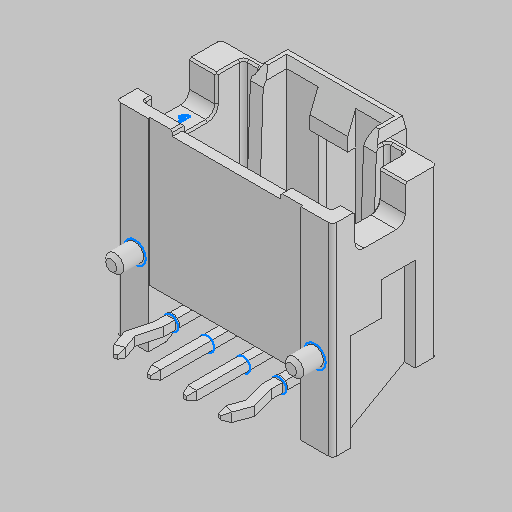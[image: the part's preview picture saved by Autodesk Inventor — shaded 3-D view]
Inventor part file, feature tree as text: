
AUTODESK INVENTOR PART (.ipt)
format: ipt  version: 2023.5 (Build 275446000, 446)  size: 349,696 bytes
history: native  units: in
note: dims shown in document units (in); Inventor stores cm internally (conversion verified against a paired STEP export)
features: other x1, extrude x1, sketch x1, imported_body x1
ambient origin geometry x8: Origin, YZ Plane, XZ Plane, XY Plane, X Axis, Y Axis, Z Axis, Center Point
bodies: Solid1 (feature_tree)
feature tree (4):
  other  "Repaired Geometry1"
  extrude  "Extrusion1"  Depth=0.0039in TaperAngle=0.0deg
  sketch  "3D Sketch1"
  imported_body  "Base1"
